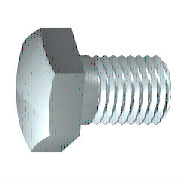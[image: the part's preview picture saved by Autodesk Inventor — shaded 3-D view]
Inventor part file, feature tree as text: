
AUTODESK INVENTOR PART (.ipt)
format: ipt  version: 2023.1 (Build 271208000, 208)  size: 198,144 bytes
history: native  units: mm (DEFAULTED — no unit token found)
features: sketch x3, extrude x1, chamfer x1, plane x1
ambient origin geometry x7: Origin, YZ Plane, XZ Plane, X Axis, Y Axis, Z Axis, Center Point
bodies: Solid1 (feature_tree), Body (feature_tree)
feature tree (6):
  extrude  "Head"  Depth=114.0mm
  chamfer  "Chamfer1"  Distance=9.2mm
  plane  "Work Plane1"
  sketch  "Sketch1"  dims[d0=120.0mm d1=114.0mm]
  sketch  "Sketch2"  dims[d2=16.0mm]
  sketch  "Sketch4"  dims[d12=90.0deg d3=9.2mm d4=0.0mm d5=30.0deg d21=90.0deg d6=1.2269mm d7=1.227mm d8=0.0mm d9=0.8001mm d10=22.49mm d11=24.0mm d13=1.227mm d14=16.0mm d15=114.0mm d16=0.0mm d19=24.0mm d55=45.0deg d57=0.0mm d58=0.0mm]
